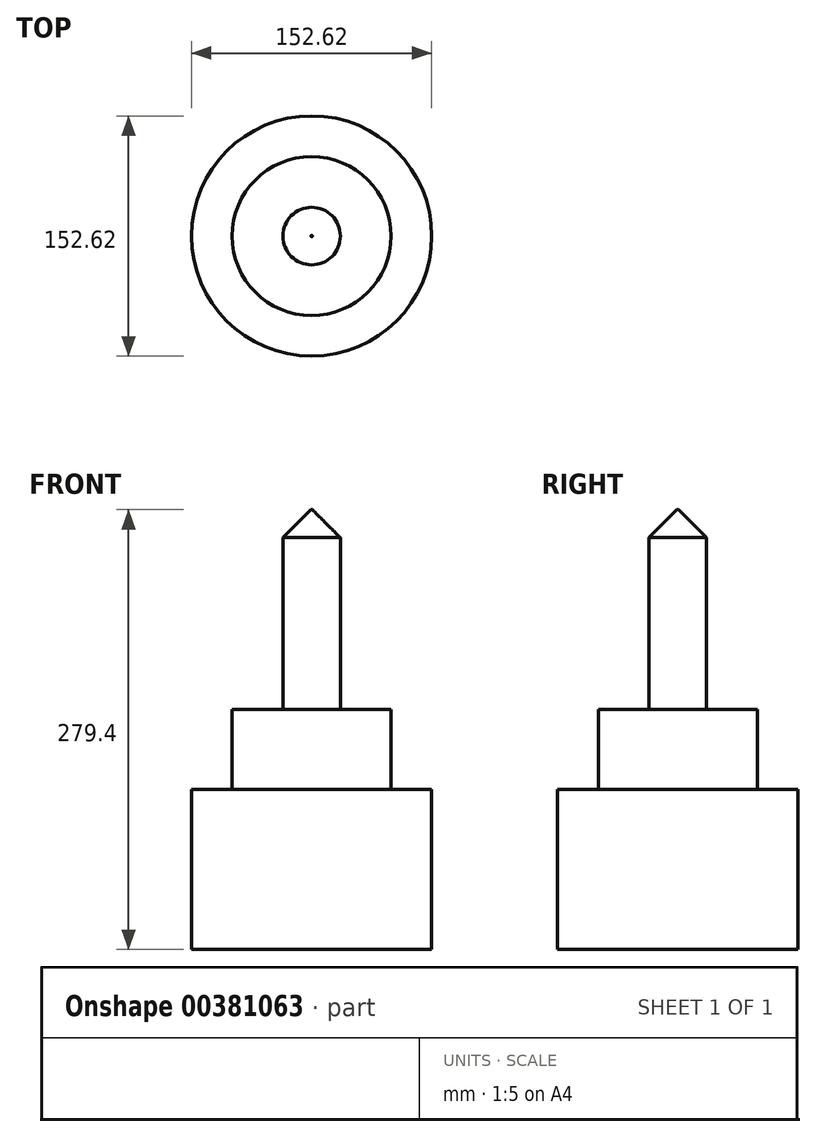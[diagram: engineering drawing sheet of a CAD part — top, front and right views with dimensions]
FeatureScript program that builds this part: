
annotation { "Feature Type Name" : "Feature", "Feature Type Description" : "" }
export const myFeature = defineFeature(function(context is Context, id is Id, definition is map)
    precondition{}
    {
        {
            var Q0;
            Q0=qCreatedBy(makeId("Top.planeOp"),FACE);
            var sketch = newSketch(context, id + "F0", { "sketchPlane" : qUnion([Q0])});
            skCircle(sketch, "E0", {"center": v(0, 0) * mm, "radius": 76.3 * mm});
            skSolve(sketch);
        }
        {
            var Q0;
            Q0 = qSketchRegion(id + "F0", true);
            extrude(context, id + "F1", {"entities" : qUnion([Q0]), "depth" : 101.6 * mm});
        }
        {
            var Q0;
            Q0=makeQuery(id+"F1.opExtrude","CAP_FACE",FACE,{"disambiguationData":[OSD([sQuery(id+"F0.wireOp",EDGE,"E0")])],"isStart":false});
            var sketch = newSketch(context, id + "F2", { "sketchPlane" : qUnion([Q0])});
            skCircle(sketch, "E1", {"center": v(0, 0) * mm, "radius": 50.46 * mm});
            skSolve(sketch);
        }
        {
            var Q0;
            Q0 = qSketchRegion(id + "F2", true);
            extrude(context, id + "F3", {"entities" : qUnion([Q0]), "operationType" : NewBodyOperationType.ADD, "depth" : 50.8 * mm});
        }
        {
            var Q0;
            Q0=makeQuery(id+"F3.opExtrude","CAP_FACE",FACE,{"disambiguationData":[OSD([sQuery(id+"F2.wireOp",EDGE,"E1")])],"isStart":false});
            var sketch = newSketch(context, id + "F4", { "sketchPlane" : qUnion([Q0])});
            skCircle(sketch, "E2", {"center": v(0, 0) * mm, "radius": 18.27 * mm});
            skSolve(sketch);
        }
        {
            var Q0;
            Q0 = qSketchRegion(id + "F4", true);
            extrude(context, id + "F5", {"entities" : qUnion([Q0]), "operationType" : NewBodyOperationType.ADD, "depth" : 127 * mm});
        }
        {
            var Q0;
            Q0=makeQuery(id+"F5.opExtrude","CAP_EDGE",EDGE,{"disambiguationData":[OSD([sQuery(id+"F4.wireOp",EDGE,"E2")])],"isStart":false});
            chamfer(context, id + "F6", {"entities" : qUnion([Q0]), "width" : 17.78 * mm, "tangentPropagation" : true});
        }
    });
